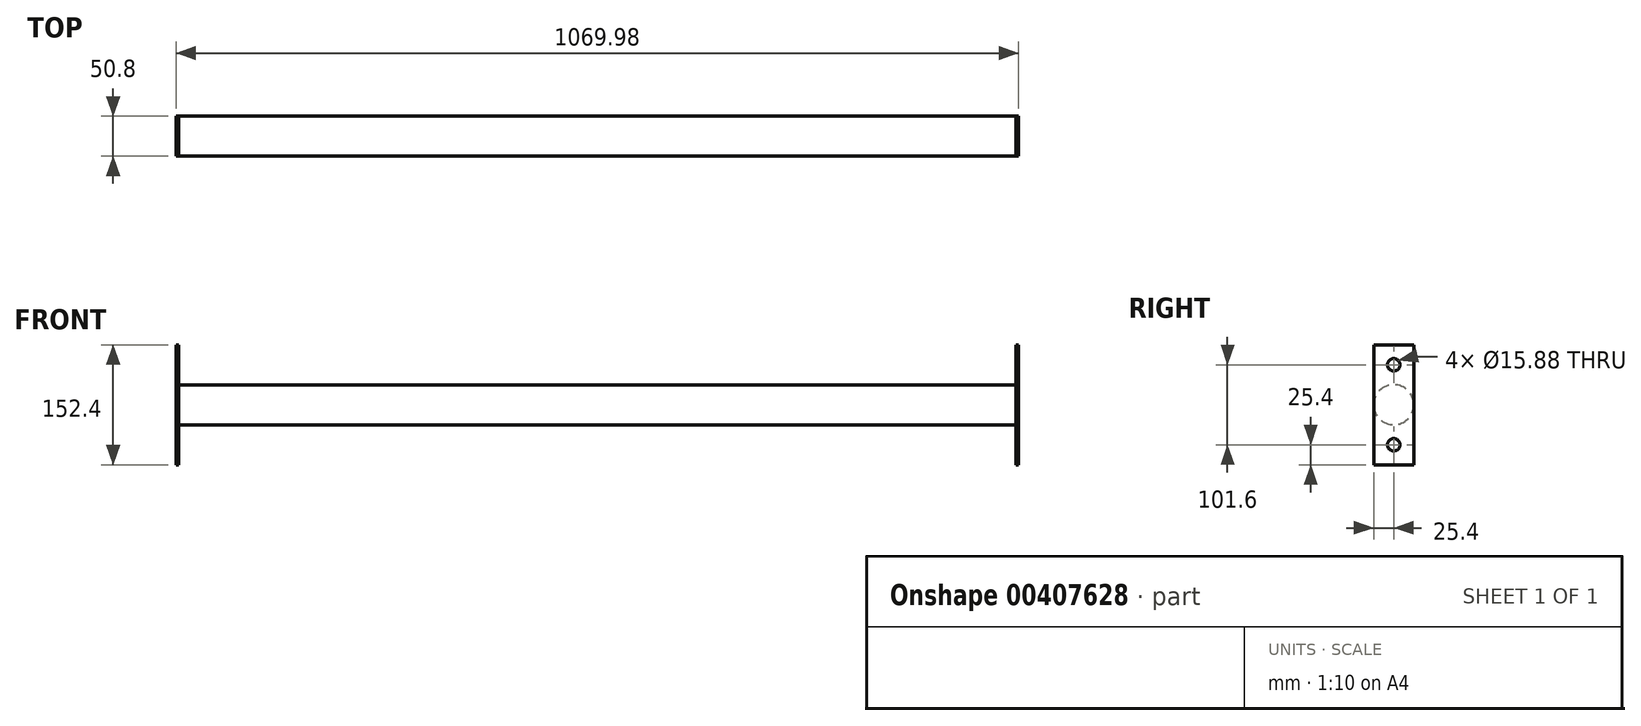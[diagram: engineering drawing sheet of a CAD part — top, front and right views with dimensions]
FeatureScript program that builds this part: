
annotation { "Feature Type Name" : "Feature", "Feature Type Description" : "" }
export const myFeature = defineFeature(function(context is Context, id is Id, definition is map)
    precondition{}
    {
        {
            var Q0;
            Q0=qCreatedBy(makeId("Right.planeOp"),FACE);
            var sketch = newSketch(context, id + "F0", { "sketchPlane" : qUnion([Q0])});
            skCircle(sketch, "E0", {"center": v(0, 0) * mm, "radius": 25.4 * mm});
            skSolve(sketch);
        }
        {
            var Q0;
            Q0 = qSketchRegion(id + "F0", true);
            extrude(context, id + "F1", {"entities" : qUnion([Q0]), "depth" : 1069.97 * mm});
        }
        {
            var Q0;
            Q0=qCreatedBy(makeId("Right.planeOp"),FACE);
            var sketch = newSketch(context, id + "F2", { "sketchPlane" : qUnion([Q0])});
            skLineSegment(sketch, "E1.bottom", {"start": v(25.4, 76.2) * mm, "end": v(-25.4, 76.2) * mm});
            skLineSegment(sketch, "E1.top", {"start": v(25.4, -76.2) * mm, "end": v(-25.4, -76.2) * mm});
            skLineSegment(sketch, "E1.left", {"start": v(25.4, 76.2) * mm, "end": v(25.4, -76.2) * mm});
            skLineSegment(sketch, "E1.right", {"start": v(-25.4, 76.2) * mm, "end": v(-25.4, -76.2) * mm});
            skSolve(sketch);
        }
        {
            var Q0;
            Q0 = qSketchRegion(id + "F2", true);
            extrude(context, id + "F3", {"entities" : qUnion([Q0]), "operationType" : NewBodyOperationType.ADD, "depth" : 3.17 * mm, "offsetDistance" : 25.4 * mm});
        }
        {
            var Q0;
            Q0=makeQuery(id+"F3.boolean.opBoolean","MERGE",FACE,{"derivedFrom":[makeQuery(id+"F1.opExtrude","CAP_FACE",FACE,{"disambiguationData":[OSD([sQuery(id+"F0.wireOp",EDGE,"E0")])],"isStart":true}),makeQuery(id+"F3.opExtrude","CAP_FACE",FACE,{"disambiguationData":[OSD([sQuery(id+"F2.wireOp",EDGE,"E1.bottom"),sQuery(id+"F2.wireOp",EDGE,"E1.top"),sQuery(id+"F2.wireOp",EDGE,"E1.left"),sQuery(id+"F2.wireOp",EDGE,"E1.right")])],"isStart":true})]});
            var sketch = newSketch(context, id + "F4", { "sketchPlane" : qUnion([Q0])});
            skPoint(sketch, "E2", {"position": v(0, 50.8) * mm});
            skPoint(sketch, "E3", {"position": v(0, -50.8) * mm});
            skSolve(sketch);
        }
        {
            var Q0;
            Q0=sQuery(id+"F4.wireOp",VERTEX,"E2");
            var Q1;
            Q1=sQuery(id+"F4.wireOp",VERTEX,"E3");
            var Q2;
            Q2=makeQuery(id+"F1.opExtrude","SWEPT_BODY",BODY,{"disambiguationData":[OSD([sQuery(id+"F0.wireOp",EDGE,"E0")])]});
            hole(context, id + "F5", {"style" : HoleStyle.SIMPLE, "endStyle" : HoleEndStyle.THROUGH, "holeDiameter" : 15.88 * mm, "majorDiameter" : 6.35 * mm, "isTappedThrough" : true, "tappedDepth" : 12.7 * mm, "tapClearance" : 3, "locations" : qUnion([Q0, Q1]), "scope" : qUnion([Q2]), "startStyle" : HoleStartStyle.PART});
        }
        {
            var Q0;
            Q0=makeQuery(id+"F1.opExtrude","CAP_FACE",FACE,{"disambiguationData":[OSD([sQuery(id+"F0.wireOp",EDGE,"E0")])],"isStart":false});
            var sketch = newSketch(context, id + "F6", { "sketchPlane" : qUnion([Q0])});
            skLineSegment(sketch, "E4.0", {"start": v(25.4, 76.2) * mm, "end": v(-25.4, 76.2) * mm});
            skLineSegment(sketch, "E5.0", {"start": v(-25.4, 76.2) * mm, "end": v(-25.4, 0) * mm});
            skLineSegment(sketch, "E6.0", {"start": v(-25.4, 0) * mm, "end": v(-25.4, -76.2) * mm});
            skLineSegment(sketch, "E7.0", {"start": v(25.4, -76.2) * mm, "end": v(-25.4, -76.2) * mm});
            skLineSegment(sketch, "E8.0", {"start": v(25.4, 0) * mm, "end": v(25.4, -76.2) * mm});
            skLineSegment(sketch, "E9.0", {"start": v(25.4, 76.2) * mm, "end": v(25.4, 0) * mm});
            skSolve(sketch);
        }
        {
            var Q0;
            Q0 = qSketchRegion(id + "F6", true);
            extrude(context, id + "F7", {"entities" : qUnion([Q0]), "operationType" : NewBodyOperationType.ADD, "oppositeDirection" : true, "depth" : 3.17 * mm, "offsetDistance" : 25.4 * mm});
        }
        {
            var Q0;
            Q0=makeQuery(id+"F7.boolean.opBoolean","MERGE",FACE,{"derivedFrom":[makeQuery(id+"F1.opExtrude","CAP_FACE",FACE,{"disambiguationData":[OSD([sQuery(id+"F0.wireOp",EDGE,"E0")])],"isStart":false}),makeQuery(id+"F7.opExtrude","CAP_FACE",FACE,{"disambiguationData":[OSD([sQuery(id+"F6.wireOp",EDGE,"E4.0"),sQuery(id+"F6.wireOp",EDGE,"E5.0"),sQuery(id+"F6.wireOp",EDGE,"E6.0"),sQuery(id+"F6.wireOp",EDGE,"E7.0"),sQuery(id+"F6.wireOp",EDGE,"E8.0"),sQuery(id+"F6.wireOp",EDGE,"E9.0")])],"isStart":true})]});
            var sketch = newSketch(context, id + "F8", { "sketchPlane" : qUnion([Q0])});
            skPoint(sketch, "E10", {"position": v(0, 50.8) * mm});
            skPoint(sketch, "E11", {"position": v(0, -50.8) * mm});
            skSolve(sketch);
        }
        {
            var Q0;
            Q0=sQuery(id+"F8.wireOp",VERTEX,"E10");
            var Q1;
            Q1=sQuery(id+"F8.wireOp",VERTEX,"E11");
            var Q2;
            Q2=makeQuery(id+"F1.opExtrude","SWEPT_BODY",BODY,{"disambiguationData":[OSD([sQuery(id+"F0.wireOp",EDGE,"E0")])]});
            hole(context, id + "F9", {"style" : HoleStyle.SIMPLE, "endStyle" : HoleEndStyle.THROUGH, "holeDiameter" : 15.88 * mm, "majorDiameter" : 6.35 * mm, "isTappedThrough" : true, "tappedDepth" : 12.7 * mm, "tapClearance" : 3, "locations" : qUnion([Q0, Q1]), "scope" : qUnion([Q2]), "startStyle" : HoleStartStyle.PART});
        }
    });
